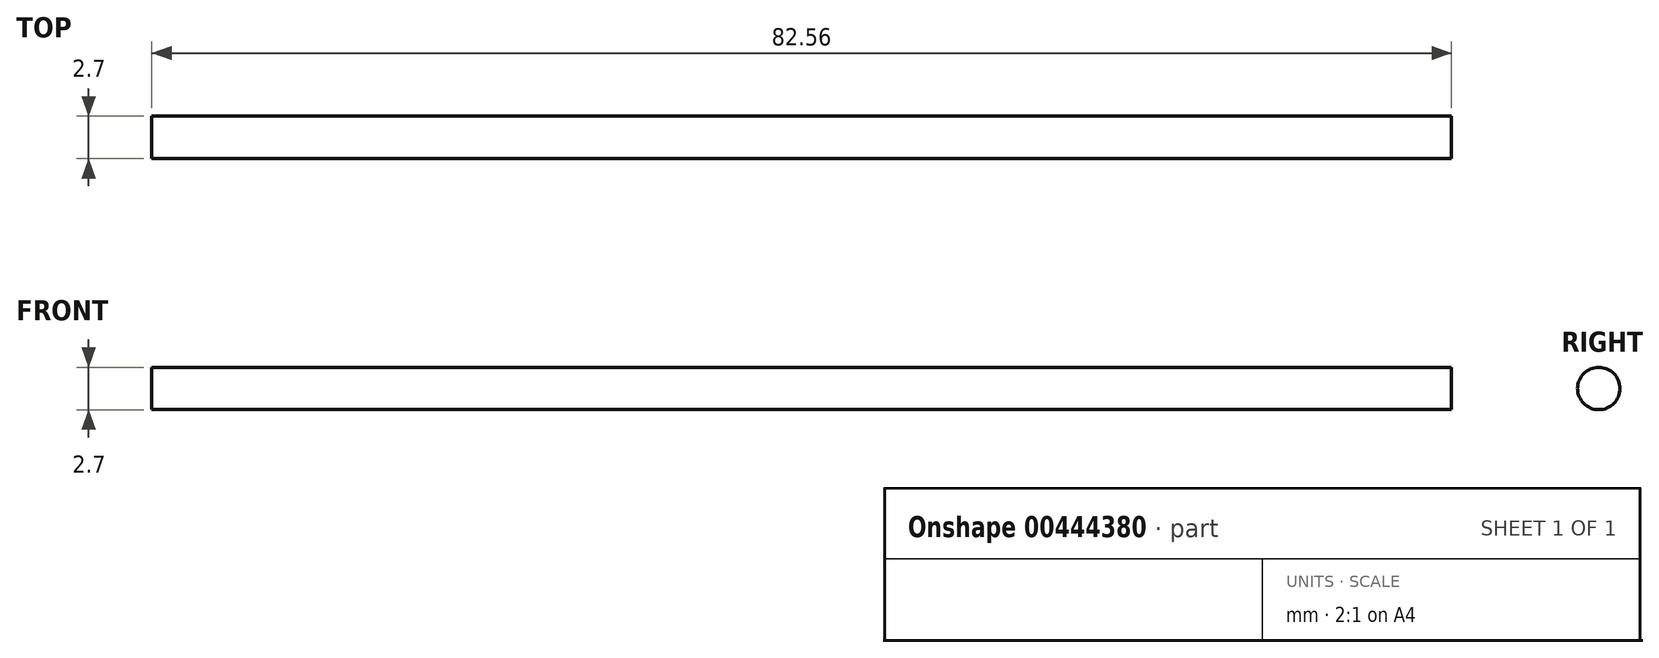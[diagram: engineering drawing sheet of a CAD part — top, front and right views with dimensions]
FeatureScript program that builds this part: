
annotation { "Feature Type Name" : "Feature", "Feature Type Description" : "" }
export const myFeature = defineFeature(function(context is Context, id is Id, definition is map)
    precondition{}
    {
        {
            var Q0;
            Q0=qCreatedBy(makeId("Right.planeOp"),FACE);
            var sketch = newSketch(context, id + "F0", { "sketchPlane" : qUnion([Q0])});
            skCircle(sketch, "E0", {"center": v(0, 0) * mm, "radius": 1.35 * mm});
            skSolve(sketch);
        }
        {
            var Q0;
            Q0 = qSketchRegion(id + "F0", true);
            extrude(context, id + "F1", {"entities" : qUnion([Q0]), "endBound" : BoundingType.SYMMETRIC, "depth" : 82.55 * mm});
        }
    });
